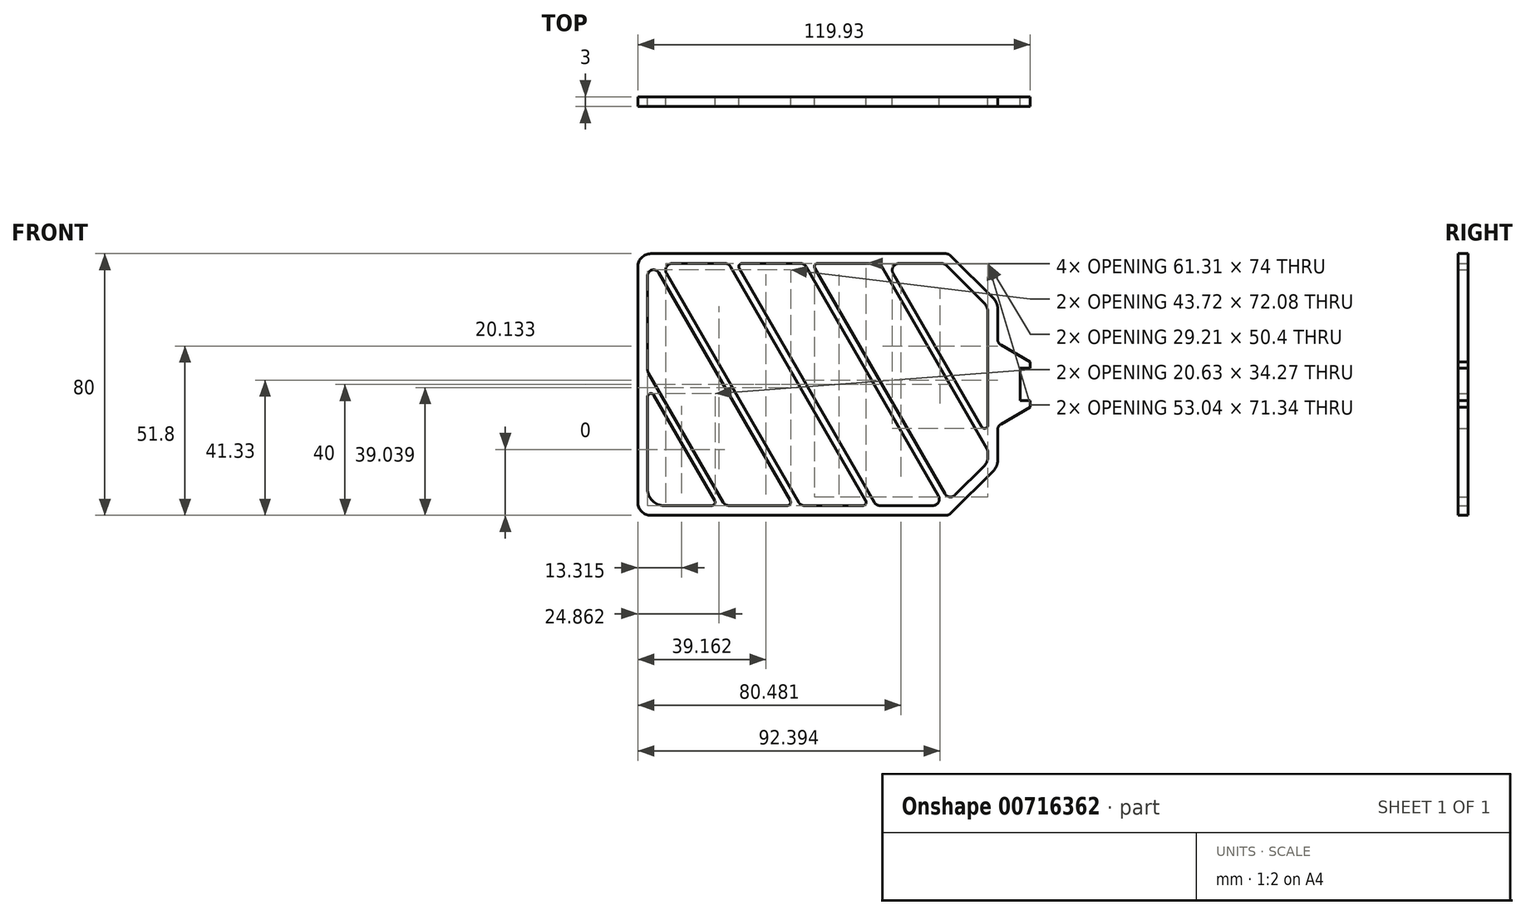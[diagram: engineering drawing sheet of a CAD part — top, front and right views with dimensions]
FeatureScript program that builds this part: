
annotation { "Feature Type Name" : "Feature", "Feature Type Description" : "" }
export const myFeature = defineFeature(function(context is Context, id is Id, definition is map)
    precondition{}
    {
        {
            var Q0;
            Q0=qCreatedBy(makeId("Front.planeOp"),FACE);
            var sketch = newSketch(context, id + "F0", { "sketchPlane" : qUnion([Q0])});
            skLineSegment(sketch, "E0.bottom", {"start": v(-51, -40) * mm, "end": v(39.17, -40) * mm});
            skLineSegment(sketch, "E0.top", {"start": v(-51, 40) * mm, "end": v(35.76, 40) * mm});
            skLineSegment(sketch, "E0.left", {"start": v(-55, -36) * mm, "end": v(-55, 36) * mm});
            skLineSegment(sketch, "E0.right", {"start": v(55, -23.34) * mm, "end": v(55, -13.84) * mm});
            skPoint(sketch, "E0.middle", {"position": v(0, 0) * mm});
            skLineSegment(sketch, "E1.0", {"start": v(-44.5, 37) * mm, "end": v(-28.33, 37) * mm});
            skLineSegment(sketch, "E1.1", {"start": v(-52, -32) * mm, "end": v(-52, -3.73) * mm});
            skLineSegment(sketch, "E1.2", {"start": v(-47, -37) * mm, "end": v(-32.37, -37) * mm});
            skLineSegment(sketch, "E1.3", {"start": v(52, -22.1) * mm, "end": v(52, -20.67) * mm});
            skLineSegment(sketch, "E2", {"start": v(-50.13, -3.23) * mm, "end": v(-31.5, -35.5) * mm});
            skLineSegment(sketch, "E3.0", {"start": v(-51.73, 3.54) * mm, "end": v(-28.9, -36) * mm});
            skLineSegment(sketch, "E4.0", {"start": v(-48.64, 34.18) * mm, "end": v(-8.41, -35.5) * mm});
            skLineSegment(sketch, "E5.0", {"start": v(-46.23, 34) * mm, "end": v(-5.81, -36) * mm});
            skLineSegment(sketch, "E6.0", {"start": v(-26.6, 36) * mm, "end": v(14.68, -35.5) * mm});
            skLineSegment(sketch, "E7.0", {"start": v(-24, 35.5) * mm, "end": v(17.28, -36) * mm});
            skLineSegment(sketch, "E8.0", {"start": v(-3.5, 36) * mm, "end": v(36.91, -34) * mm});
            skLineSegment(sketch, "E9.0", {"start": v(-0.9, 35.5) * mm, "end": v(38.85, -33.35) * mm});
            skLineSegment(sketch, "E10.0", {"start": v(19.3, 36.5) * mm, "end": v(51.73, -19.67) * mm});
            skLineSegment(sketch, "E11.0", {"start": v(23.06, 34) * mm, "end": v(50.13, -12.9) * mm});
            skLineSegment(sketch, "E12.left", {"start": v(61.93, 5) * mm, "end": v(61.93, -4.95) * mm});
            skPoint(sketch, "E12.middle", {"position": v(55, 0) * mm});
            skLineSegment(sketch, "E13", {"start": v(61.93, -4.95) * mm, "end": v(64.93, -4.95) * mm});
            skLineSegment(sketch, "E14", {"start": v(64.93, -4.95) * mm, "end": v(64.93, -6.95) * mm});
            skLineSegment(sketch, "E15", {"start": v(64.93, -6.95) * mm, "end": v(56, -12.1) * mm});
            skLineSegment(sketch, "E16.MirrorCS", {"start": v(64.93, 6.95) * mm, "end": v(56, 12.1) * mm});
            skLineSegment(sketch, "E17.MirrorCS", {"start": v(64.93, 4.95) * mm, "end": v(64.93, 6.95) * mm});
            skLineSegment(sketch, "E18.MirrorCS", {"start": v(61.93, 4.95) * mm, "end": v(64.93, 4.95) * mm});
            skLineSegment(sketch, "E19", {"start": v(40.59, 39.41) * mm, "end": v(53.83, 26.17) * mm});
            skLineSegment(sketch, "E20", {"start": v(40.59, -39.41) * mm, "end": v(53.83, -26.17) * mm});
            skLineSegment(sketch, "E21.0", {"start": v(39.34, 36.41) * mm, "end": v(50.83, 24.93) * mm});
            skPoint(sketch, "E22.orphan", {"position": v(55, 40) * mm});
            skPoint(sketch, "E23.orphan", {"position": v(55, -40) * mm});
            skLineSegment(sketch, "E24", {"start": v(39.17, 40) * mm, "end": v(35.76, 40) * mm});
            skPoint(sketch, "E12.right.start.orphan", {"position": v(48.07, 4.95) * mm});
            skPoint(sketch, "E25.orphan", {"position": v(48.07, -5) * mm});
            skLineSegment(sketch, "E26.trimOffspring", {"start": v(55, 13.84) * mm, "end": v(55, 23.34) * mm});
            skLineSegment(sketch, "E27.trimOffspring", {"start": v(52, -12.4) * mm, "end": v(52, 22.1) * mm});
            skLineSegment(sketch, "E28.trimOffspring", {"start": v(42, -33.76) * mm, "end": v(50.83, -24.93) * mm});
            skLineSegment(sketch, "E29.trimOffspring", {"start": v(24.79, 37) * mm, "end": v(37.93, 37) * mm});
            skLineSegment(sketch, "E30.trimOffspring", {"start": v(-0.04, 37) * mm, "end": v(18.44, 37) * mm});
            skLineSegment(sketch, "E31.trimOffspring", {"start": v(-23.13, 37) * mm, "end": v(-5.23, 37) * mm});
            skPoint(sketch, "E32.orphan", {"position": v(-52, 37) * mm});
            skLineSegment(sketch, "E33.trimOffspring", {"start": v(-52, 4.54) * mm, "end": v(-52, 33.28) * mm});
            skLineSegment(sketch, "E34.trimOffspring", {"start": v(-27.17, -37) * mm, "end": v(-9.28, -37) * mm});
            skLineSegment(sketch, "E35.trimOffspring", {"start": v(-4.08, -37) * mm, "end": v(13.82, -37) * mm});
            skLineSegment(sketch, "E36.trimOffspring", {"start": v(19.01, -37) * mm, "end": v(35.18, -37) * mm});
            skPoint(sketch, "E37.visualSharp", {"position": v(21.32, 37) * mm});
            skArc(sketch, "E37.filletArc", {"start": v(24.79, 37) * mm, "mid": v(23.06, 36) * mm, "end": v(23.06, 34) * mm});
            skPoint(sketch, "E38.visualSharp", {"position": v(19.01, 37) * mm});
            skArc(sketch, "E38.filletArc", {"start": v(19.3, 36.5) * mm, "mid": v(18.94, 36.87) * mm, "end": v(18.44, 37) * mm});
            skPoint(sketch, "E39.visualSharp", {"position": v(-1.77, 37) * mm});
            skArc(sketch, "E39.filletArc", {"start": v(-0.04, 37) * mm, "mid": v(-0.9, 36.5) * mm, "end": v(-0.9, 35.5) * mm});
            skPoint(sketch, "E40.visualSharp", {"position": v(-4.08, 37) * mm});
            skArc(sketch, "E40.filletArc", {"start": v(-3.5, 36) * mm, "mid": v(-4.23, 36.73) * mm, "end": v(-5.23, 37) * mm});
            skPoint(sketch, "E41.visualSharp", {"position": v(-27.17, 37) * mm});
            skArc(sketch, "E41.filletArc", {"start": v(-26.6, 36) * mm, "mid": v(-27.33, 36.73) * mm, "end": v(-28.33, 37) * mm});
            skPoint(sketch, "E42.visualSharp", {"position": v(-24.86, 37) * mm});
            skArc(sketch, "E42.filletArc", {"start": v(-23.13, 37) * mm, "mid": v(-24, 36.5) * mm, "end": v(-24, 35.5) * mm});
            skPoint(sketch, "E43.visualSharp", {"position": v(-47.96, 37) * mm});
            skArc(sketch, "E43.filletArc", {"start": v(-44.5, 37) * mm, "mid": v(-46.23, 36) * mm, "end": v(-46.23, 34) * mm});
            skPoint(sketch, "E44.visualSharp", {"position": v(-52, 40) * mm});
            skArc(sketch, "E44.filletArc", {"start": v(-48.64, 34.18) * mm, "mid": v(-50.67, 35.02) * mm, "end": v(-52, 33.28) * mm});
            skPoint(sketch, "E45.visualSharp", {"position": v(-52, 4) * mm});
            skArc(sketch, "E45.filletArc", {"start": v(-52, 4.54) * mm, "mid": v(-51.93, 4.02) * mm, "end": v(-51.73, 3.54) * mm});
            skPoint(sketch, "E46.visualSharp", {"position": v(-52, 0) * mm});
            skArc(sketch, "E46.filletArc", {"start": v(-50.13, -3.23) * mm, "mid": v(-51.26, -2.77) * mm, "end": v(-52, -3.73) * mm});
            skPoint(sketch, "E47.visualSharp", {"position": v(-30.64, -37) * mm});
            skArc(sketch, "E47.filletArc", {"start": v(-32.37, -37) * mm, "mid": v(-31.5, -36.5) * mm, "end": v(-31.5, -35.5) * mm});
            skPoint(sketch, "E48.visualSharp", {"position": v(-28.33, -37) * mm});
            skArc(sketch, "E48.filletArc", {"start": v(-28.9, -36) * mm, "mid": v(-28.17, -36.73) * mm, "end": v(-27.17, -37) * mm});
            skPoint(sketch, "E49.visualSharp", {"position": v(-7.54, -37) * mm});
            skArc(sketch, "E49.filletArc", {"start": v(-9.28, -37) * mm, "mid": v(-8.41, -36.5) * mm, "end": v(-8.41, -35.5) * mm});
            skPoint(sketch, "E50.visualSharp", {"position": v(-5.23, -37) * mm});
            skArc(sketch, "E50.filletArc", {"start": v(-5.81, -36) * mm, "mid": v(-5.08, -36.73) * mm, "end": v(-4.08, -37) * mm});
            skPoint(sketch, "E51.visualSharp", {"position": v(15.55, -37) * mm});
            skArc(sketch, "E51.filletArc", {"start": v(13.82, -37) * mm, "mid": v(14.68, -36.5) * mm, "end": v(14.68, -35.5) * mm});
            skPoint(sketch, "E52.visualSharp", {"position": v(17.86, -37) * mm});
            skArc(sketch, "E52.filletArc", {"start": v(17.28, -36) * mm, "mid": v(18.01, -36.73) * mm, "end": v(19.01, -37) * mm});
            skPoint(sketch, "E53.visualSharp", {"position": v(38.69, -37.07) * mm});
            skPoint(sketch, "E54.visualSharp", {"position": v(40.15, -35.6) * mm});
            skArc(sketch, "E54.filletArc", {"start": v(38.85, -33.35) * mm, "mid": v(40.32, -34.33) * mm, "end": v(42, -33.76) * mm});
            skPoint(sketch, "E55.visualSharp", {"position": v(52, -20.13) * mm});
            skArc(sketch, "E55.filletArc", {"start": v(52, -20.67) * mm, "mid": v(51.93, -20.15) * mm, "end": v(51.73, -19.67) * mm});
            skPoint(sketch, "E56.visualSharp", {"position": v(52, -16.13) * mm});
            skArc(sketch, "E56.filletArc", {"start": v(50.13, -12.9) * mm, "mid": v(51.26, -13.37) * mm, "end": v(52, -12.4) * mm});
            skPoint(sketch, "E57.visualSharp", {"position": v(55, -12.68) * mm});
            skArc(sketch, "E57.filletArc", {"start": v(56, -12.1) * mm, "mid": v(55.27, -12.84) * mm, "end": v(55, -13.84) * mm});
            skPoint(sketch, "E58.visualSharp", {"position": v(55, -25) * mm});
            skArc(sketch, "E58.filletArc", {"start": v(53.83, -26.17) * mm, "mid": v(54.7, -24.87) * mm, "end": v(55, -23.34) * mm});
            skArc(sketch, "E59.filletArc", {"start": v(39.17, -40) * mm, "mid": v(39.94, -39.85) * mm, "end": v(40.59, -39.41) * mm});
            skPoint(sketch, "E60.visualSharp", {"position": v(55, 12.68) * mm});
            skArc(sketch, "E60.filletArc", {"start": v(55, 13.84) * mm, "mid": v(55.27, 12.84) * mm, "end": v(56, 12.1) * mm});
            skPoint(sketch, "E61.visualSharp", {"position": v(55, 25) * mm});
            skArc(sketch, "E61.filletArc", {"start": v(55, 23.34) * mm, "mid": v(54.7, 24.87) * mm, "end": v(53.83, 26.17) * mm});
            skPoint(sketch, "E62.visualSharp", {"position": v(40, 40) * mm});
            skArc(sketch, "E62.filletArc", {"start": v(40.59, 39.41) * mm, "mid": v(39.94, 39.85) * mm, "end": v(39.17, 40) * mm});
            skPoint(sketch, "E63.visualSharp", {"position": v(38.76, 37) * mm});
            skArc(sketch, "E63.filletArc", {"start": v(39.34, 36.41) * mm, "mid": v(38.7, 36.85) * mm, "end": v(37.93, 37) * mm});
            skPoint(sketch, "E64.visualSharp", {"position": v(52, 23.76) * mm});
            skArc(sketch, "E64.filletArc", {"start": v(52, 22.1) * mm, "mid": v(51.7, 23.63) * mm, "end": v(50.83, 24.93) * mm});
            skPoint(sketch, "E65.visualSharp", {"position": v(52, -23.76) * mm});
            skArc(sketch, "E65.filletArc", {"start": v(50.83, -24.93) * mm, "mid": v(51.7, -23.63) * mm, "end": v(52, -22.1) * mm});
            skPoint(sketch, "E66.visualSharp", {"position": v(-55, 40) * mm});
            skArc(sketch, "E66.filletArc", {"start": v(-51, 40) * mm, "mid": v(-53.83, 38.83) * mm, "end": v(-55, 36) * mm});
            skPoint(sketch, "E67.visualSharp", {"position": v(-55, -40) * mm});
            skArc(sketch, "E67.filletArc", {"start": v(-55, -36) * mm, "mid": v(-53.83, -38.83) * mm, "end": v(-51, -40) * mm});
            skPoint(sketch, "E68.visualSharp", {"position": v(-52, -37) * mm});
            skArc(sketch, "E68.filletArc", {"start": v(-52, -32) * mm, "mid": v(-50.54, -35.54) * mm, "end": v(-47, -37) * mm});
            skPoint(sketch, "E69.visualSharp", {"position": v(38.64, -37) * mm});
            skArc(sketch, "E69.filletArc", {"start": v(35.18, -37) * mm, "mid": v(36.91, -36) * mm, "end": v(36.91, -34) * mm});
            skSolve(sketch);
        }
        {
            var Q0;
            Q0=makeQuery(id+"F0.imprint","IMPRINT",FACE,{"disambiguationData":[TD([[makeQuery(id+"F0.imprint","IMPRINT",EDGE,{"derivedFrom":sQuery(id+"F0.wireOp",EDGE,"E0.bottom")}),1.0]])]});
            extrude(context, id + "F1", {"entities" : qUnion([Q0]), "depth" : 3 * mm, "offsetDistance" : 25 * mm});
        }
    });
